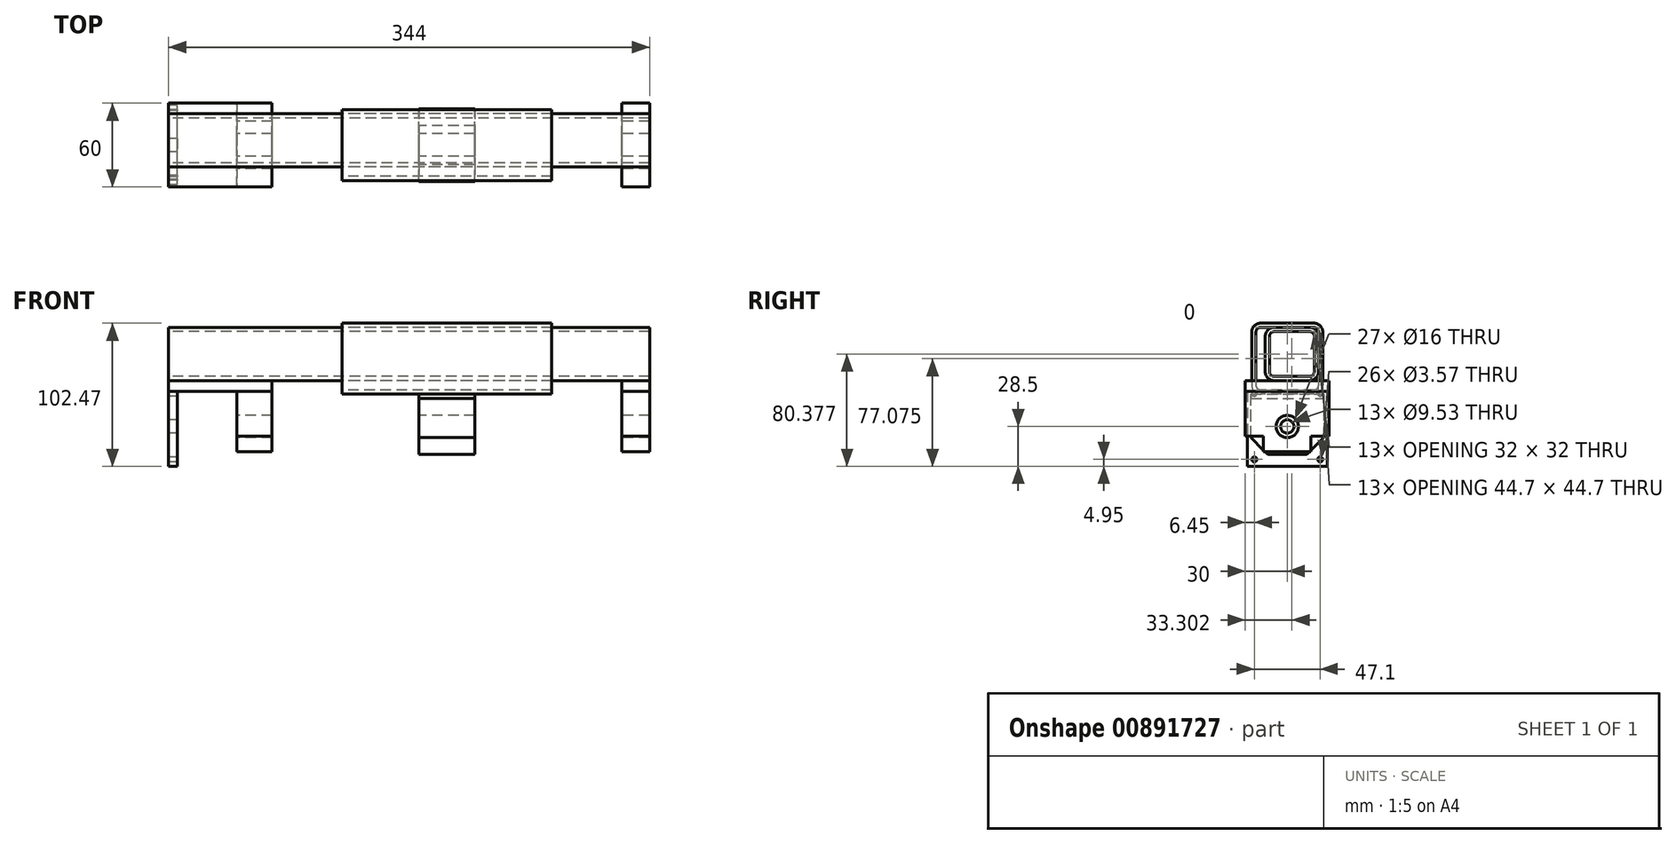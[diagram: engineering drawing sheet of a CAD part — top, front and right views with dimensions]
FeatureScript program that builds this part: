
annotation { "Feature Type Name" : "Feature", "Feature Type Description" : "" }
export const myFeature = defineFeature(function(context is Context, id is Id, definition is map)
    precondition{}
    {
        {
            var Q0;
            Q0=qCreatedBy(makeId("Right.planeOp"),FACE);
            var sketch = newSketch(context, id + "F0", { "sketchPlane" : qUnion([Q0])});
            skLineSegment(sketch, "E0", {"start": v(-26, 20) * mm, "end": v(26, 20) * mm});
            skLineSegment(sketch, "E1", {"start": v(26, 20) * mm, "end": v(26, -7.98) * mm});
            skLineSegment(sketch, "E2", {"start": v(26, -7.98) * mm, "end": v(13.98, -20) * mm});
            skLineSegment(sketch, "E3", {"start": v(13.98, -20) * mm, "end": v(-13.98, -20) * mm});
            skLineSegment(sketch, "E4", {"start": v(-13.98, -20) * mm, "end": v(-26, -7.98) * mm});
            skLineSegment(sketch, "E5", {"start": v(-26, -7.98) * mm, "end": v(-26, 20) * mm});
            skPoint(sketch, "E6", {"position": v(0, 0) * mm});
            skCircle(sketch, "E7", {"center": v(0, 0) * mm, "radius": 8 * mm});
            skSolve(sketch);
        }
        {
            var Q0;
            Q0=qCreatedBy(makeId("Right.planeOp"),FACE);
            var sketch = newSketch(context, id + "F1", { "sketchPlane" : qUnion([Q0])});
            skLineSegment(sketch, "E8.bottom", {"start": v(19.18, 70.93) * mm, "end": v(-19.18, 70.93) * mm});
            skLineSegment(sketch, "E8.top", {"start": v(19.18, 26.22) * mm, "end": v(-19.18, 26.22) * mm});
            skLineSegment(sketch, "E8.left", {"start": v(22.35, 67.75) * mm, "end": v(22.35, 29.4) * mm});
            skLineSegment(sketch, "E8.right", {"start": v(-22.35, 67.75) * mm, "end": v(-22.35, 29.4) * mm});
            skPoint(sketch, "E8.middle", {"position": v(0, 48.58) * mm});
            skLineSegment(sketch, "E9.bottom", {"start": v(19.05, 73.98) * mm, "end": v(-19.05, 73.98) * mm});
            skLineSegment(sketch, "E9.top", {"start": v(19.05, 23.18) * mm, "end": v(-19.05, 23.18) * mm});
            skLineSegment(sketch, "E9.left", {"start": v(25.4, 67.63) * mm, "end": v(25.4, 29.53) * mm});
            skLineSegment(sketch, "E9.right", {"start": v(-25.4, 67.63) * mm, "end": v(-25.4, 29.53) * mm});
            skPoint(sketch, "E10.visualSharp", {"position": v(-22.35, 70.93) * mm});
            skArc(sketch, "E10.filletArc", {"start": v(-19.18, 70.93) * mm, "mid": v(-21.42, 70) * mm, "end": v(-22.35, 67.75) * mm});
            skPoint(sketch, "E11.visualSharp", {"position": v(22.35, 70.93) * mm});
            skArc(sketch, "E11.filletArc", {"start": v(22.35, 67.75) * mm, "mid": v(21.42, 70) * mm, "end": v(19.18, 70.93) * mm});
            skPoint(sketch, "E12.visualSharp", {"position": v(22.35, 26.22) * mm});
            skArc(sketch, "E12.filletArc", {"start": v(19.18, 26.22) * mm, "mid": v(21.42, 27.15) * mm, "end": v(22.35, 29.4) * mm});
            skPoint(sketch, "E13.visualSharp", {"position": v(-22.35, 26.22) * mm});
            skArc(sketch, "E13.filletArc", {"start": v(-22.35, 29.4) * mm, "mid": v(-21.42, 27.15) * mm, "end": v(-19.18, 26.22) * mm});
            skPoint(sketch, "E14.visualSharp", {"position": v(-25.4, 73.98) * mm});
            skArc(sketch, "E14.filletArc", {"start": v(-19.05, 73.98) * mm, "mid": v(-23.54, 72.12) * mm, "end": v(-25.4, 67.63) * mm});
            skPoint(sketch, "E15.visualSharp", {"position": v(25.4, 73.98) * mm});
            skArc(sketch, "E15.filletArc", {"start": v(25.4, 67.63) * mm, "mid": v(23.54, 72.12) * mm, "end": v(19.05, 73.98) * mm});
            skPoint(sketch, "E16.visualSharp", {"position": v(25.4, 23.18) * mm});
            skArc(sketch, "E16.filletArc", {"start": v(19.05, 23.18) * mm, "mid": v(23.54, 25.03) * mm, "end": v(25.4, 29.53) * mm});
            skPoint(sketch, "E17.visualSharp", {"position": v(-25.4, 23.18) * mm});
            skArc(sketch, "E17.filletArc", {"start": v(-25.4, 29.53) * mm, "mid": v(-23.54, 25.03) * mm, "end": v(-19.05, 23.18) * mm});
            skLineSegment(sketch, "E18.bottom", {"start": v(-26, 23.18) * mm, "end": v(26, 23.18) * mm});
            skLineSegment(sketch, "E18.top", {"start": v(-26, 20) * mm, "end": v(26, 20) * mm});
            skLineSegment(sketch, "E18.left", {"start": v(-26, 23.18) * mm, "end": v(-26, 20) * mm});
            skLineSegment(sketch, "E18.right", {"start": v(26, 23.18) * mm, "end": v(26, 20) * mm});
            skSolve(sketch);
        }
        {
            var Q0;
            Q0=qCreatedBy(makeId("Right.planeOp"),FACE);
            var sketch = newSketch(context, id + "F2", { "sketchPlane" : qUnion([Q0])});
            skLineSegment(sketch, "E19.bottom", {"start": v(16.13, 67.88) * mm, "end": v(-9.52, 67.88) * mm});
            skLineSegment(sketch, "E19.top", {"start": v(16.13, 35.87) * mm, "end": v(-9.52, 35.87) * mm});
            skLineSegment(sketch, "E19.left", {"start": v(19.3, 64.7) * mm, "end": v(19.3, 39.05) * mm});
            skLineSegment(sketch, "E19.right", {"start": v(-12.7, 64.7) * mm, "end": v(-12.7, 39.05) * mm});
            skPoint(sketch, "E19.middle", {"position": v(3.3, 51.88) * mm});
            skLineSegment(sketch, "E20.bottom", {"start": v(16, 70.93) * mm, "end": v(-9.4, 70.93) * mm});
            skLineSegment(sketch, "E20.top", {"start": v(16, 32.83) * mm, "end": v(-9.4, 32.83) * mm});
            skLineSegment(sketch, "E20.left", {"start": v(22.35, 64.58) * mm, "end": v(22.35, 39.18) * mm});
            skLineSegment(sketch, "E20.right", {"start": v(-15.75, 64.58) * mm, "end": v(-15.75, 39.18) * mm});
            skPoint(sketch, "E21.visualSharp", {"position": v(-12.7, 67.88) * mm});
            skArc(sketch, "E21.filletArc", {"start": v(-9.52, 67.88) * mm, "mid": v(-11.77, 66.95) * mm, "end": v(-12.7, 64.7) * mm});
            skPoint(sketch, "E22.visualSharp", {"position": v(19.3, 67.88) * mm});
            skArc(sketch, "E22.filletArc", {"start": v(19.3, 64.7) * mm, "mid": v(18.37, 66.95) * mm, "end": v(16.13, 67.88) * mm});
            skPoint(sketch, "E23.visualSharp", {"position": v(19.3, 35.87) * mm});
            skArc(sketch, "E23.filletArc", {"start": v(16.13, 35.87) * mm, "mid": v(18.37, 36.8) * mm, "end": v(19.3, 39.05) * mm});
            skPoint(sketch, "E24.visualSharp", {"position": v(-12.7, 35.87) * mm});
            skArc(sketch, "E24.filletArc", {"start": v(-12.7, 39.05) * mm, "mid": v(-11.77, 36.8) * mm, "end": v(-9.52, 35.87) * mm});
            skPoint(sketch, "E25.visualSharp", {"position": v(-15.75, 70.93) * mm});
            skArc(sketch, "E25.filletArc", {"start": v(-9.4, 70.93) * mm, "mid": v(-13.89, 69.07) * mm, "end": v(-15.75, 64.58) * mm});
            skPoint(sketch, "E26.visualSharp", {"position": v(22.35, 70.93) * mm});
            skArc(sketch, "E26.filletArc", {"start": v(22.35, 64.58) * mm, "mid": v(20.5, 69.07) * mm, "end": v(16, 70.93) * mm});
            skPoint(sketch, "E27.visualSharp", {"position": v(22.35, 32.83) * mm});
            skArc(sketch, "E27.filletArc", {"start": v(16, 32.83) * mm, "mid": v(20.5, 34.69) * mm, "end": v(22.35, 39.18) * mm});
            skPoint(sketch, "E28.visualSharp", {"position": v(-15.75, 32.83) * mm});
            skArc(sketch, "E28.filletArc", {"start": v(-15.75, 39.18) * mm, "mid": v(-13.89, 34.69) * mm, "end": v(-9.4, 32.83) * mm});
            skSolve(sketch);
        }
        {
            var Q0;
            Q0=qCreatedBy(makeId("Right.planeOp"),FACE);
            var sketch = newSketch(context, id + "F3", { "sketchPlane" : qUnion([Q0])});
            skLineSegment(sketch, "E29", {"start": v(-30, 25) * mm, "end": v(-30, -7) * mm});
            skLineSegment(sketch, "E30", {"start": v(-30, -7) * mm, "end": v(-17, -7) * mm});
            skLineSegment(sketch, "E31", {"start": v(-17, -7) * mm, "end": v(-17, -18) * mm});
            skLineSegment(sketch, "E32", {"start": v(-17, -18) * mm, "end": v(17, -18) * mm});
            skLineSegment(sketch, "E33", {"start": v(17, -18) * mm, "end": v(17, -7) * mm});
            skLineSegment(sketch, "E34", {"start": v(17, -7) * mm, "end": v(30, -7) * mm});
            skLineSegment(sketch, "E35", {"start": v(30, 25) * mm, "end": v(30, -7) * mm});
            skPoint(sketch, "E36", {"position": v(0, 0) * mm});
            skLineSegment(sketch, "E37", {"start": v(30, 25) * mm, "end": v(-30, 25) * mm});
            skCircle(sketch, "E38", {"center": v(0, 0) * mm, "radius": 8 * mm});
            skLineSegment(sketch, "E39.top", {"start": v(30, 32.83) * mm, "end": v(-30, 32.83) * mm});
            skLineSegment(sketch, "E39.left", {"start": v(30, 25) * mm, "end": v(30, 32.83) * mm});
            skLineSegment(sketch, "E39.right", {"start": v(-30, 25) * mm, "end": v(-30, 32.83) * mm});
            skPoint(sketch, "E39.middle", {"position": v(0, 28.91) * mm});
            skSolve(sketch);
        }
        {
            var Q0;
            Q0=qCreatedBy(makeId("Right.planeOp"),FACE);
            var sketch = newSketch(context, id + "F4", { "sketchPlane" : qUnion([Q0])});
            skLineSegment(sketch, "E40.bottom", {"start": v(23.55, -23.55) * mm, "end": v(-23.55, -23.55) * mm, "construction": true});
            skLineSegment(sketch, "E40.top", {"start": v(23.55, 23.55) * mm, "end": v(-23.55, 23.55) * mm, "construction": true});
            skLineSegment(sketch, "E40.left", {"start": v(23.55, -23.55) * mm, "end": v(23.55, 23.55) * mm, "construction": true});
            skLineSegment(sketch, "E40.right", {"start": v(-23.55, -23.55) * mm, "end": v(-23.55, 23.55) * mm, "construction": true});
            skCircle(sketch, "E41", {"center": v(-23.55, -23.55) * mm, "radius": 1.79 * mm});
            skCircle(sketch, "E42", {"center": v(-23.55, 23.55) * mm, "radius": 1.79 * mm});
            skCircle(sketch, "E43", {"center": v(23.55, 23.55) * mm, "radius": 1.79 * mm});
            skCircle(sketch, "E44", {"center": v(23.55, -23.55) * mm, "radius": 1.79 * mm});
            skPoint(sketch, "E45.middle", {"position": v(0, 0) * mm});
            skCircle(sketch, "E46", {"center": v(0, 0) * mm, "radius": 4.76 * mm});
            skLineSegment(sketch, "E47", {"start": v(23.55, 23.55) * mm, "end": v(-23.55, -23.55) * mm, "construction": true});
            skLineSegment(sketch, "E48.bottom", {"start": v(28.5, 28.5) * mm, "end": v(-28.5, 28.5) * mm, "construction": true});
            skLineSegment(sketch, "E48.top", {"start": v(28.5, -28.5) * mm, "end": v(-28.5, -28.5) * mm, "construction": true});
            skLineSegment(sketch, "E48.left", {"start": v(28.5, 28.5) * mm, "end": v(28.5, -28.5) * mm, "construction": true});
            skLineSegment(sketch, "E48.right", {"start": v(-28.5, 28.5) * mm, "end": v(-28.5, -28.5) * mm, "construction": true});
            skLineSegment(sketch, "E49.bottom", {"start": v(-28.5, 25) * mm, "end": v(28.5, 25) * mm});
            skLineSegment(sketch, "E49.top", {"start": v(-28.5, -28.5) * mm, "end": v(28.5, -28.5) * mm});
            skLineSegment(sketch, "E49.left", {"start": v(-28.5, 25) * mm, "end": v(-28.5, -28.5) * mm});
            skLineSegment(sketch, "E49.right", {"start": v(28.5, 25) * mm, "end": v(28.5, -28.5) * mm});
            skPoint(sketch, "E50", {"position": v(0, 31.35) * mm});
            skPoint(sketch, "E50.positionSnap0", {"position": v(0, 28.5) * mm});
            skSolve(sketch);
        }
        {
            var Q0;
            Q0=qCreatedBy(makeId("Front.planeOp"),FACE);
            var sketch = newSketch(context, id + "F5", { "sketchPlane" : qUnion([Q0])});
            skPoint(sketch, "E51", {"position": v(6.35, 0) * mm});
            skPoint(sketch, "E52", {"position": v(49, 0) * mm});
            skPoint(sketch, "E53", {"position": v(74, 0) * mm});
            skPoint(sketch, "E54", {"position": v(124, 0) * mm});
            skPoint(sketch, "E55", {"position": v(274, 0) * mm});
            skPoint(sketch, "E56", {"position": v(179, 0) * mm});
            skPoint(sketch, "E57", {"position": v(219, 0) * mm});
            skPoint(sketch, "E58", {"position": v(324, 0) * mm});
            skPoint(sketch, "E59", {"position": v(344, 0) * mm});
            skSolve(sketch);
        }
        {
            var Q0;
            Q0=makeQuery(id+"F4.imprint","IMPRINT",FACE,{"disambiguationData":[TD([[makeQuery(id+"F4.imprint","IMPRINT",EDGE,{"derivedFrom":sQuery(id+"F4.wireOp",EDGE,"E41")}),-1.0]])]});
            var Q1;
            Q1=sQuery(id+"F5.wireOp",VERTEX,"E51");
            extrude(context, id + "F6", {"entities" : qUnion([Q0]), "endBound" : BoundingType.UP_TO_VERTEX, "depth" : 25 * mm, "endBoundEntityVertex" : qUnion([Q1]), "offsetDistance" : 25 * mm});
        }
        {
            var Q0;
            {var subQ0=sQuery(id+"F3.wireOp",EDGE,"E29");Q0=makeQuery(id+"F3.imprint","IMPRINT",FACE,{"disambiguationData":[TD([[makeQuery(id+"F3.imprint","IMPRINT",EDGE,{"derivedFrom":subQ0}),1.0]])]});}
            var Q1;
            Q1=sQuery(id+"F5.wireOp",VERTEX,"E53");
            var Q2;
            Q2=sQuery(id+"F5.wireOp",VERTEX,"E52");
            extrude(context, id + "F7", {"entities" : qUnion([Q0]), "endBound" : BoundingType.UP_TO_VERTEX, "depth" : 25 * mm, "endBoundEntityVertex" : qUnion([Q1]), "offsetDistance" : 25 * mm, "hasSecondDirection" : true, "secondDirectionBound" : BoundingType.UP_TO_VERTEX, "secondDirectionOppositeDirection" : false, "secondDirectionDepth" : 25 * mm, "secondDirectionBoundEntityVertex" : qUnion([Q2])});
        }
        {
            var Q0;
            Q0=makeQuery(id+"F1.imprint","IMPRINT",FACE,{"disambiguationData":[TD([[makeQuery(id+"F1.imprint","IMPRINT",EDGE,{"derivedFrom":sQuery(id+"F1.wireOp",EDGE,"E8.bottom")}),-1.0]])]});
            var Q1;
            Q1=sQuery(id+"F5.wireOp",VERTEX,"E55");
            var Q2;
            Q2=sQuery(id+"F5.wireOp",VERTEX,"E54");
            extrude(context, id + "F8", {"entities" : qUnion([Q0]), "endBound" : BoundingType.UP_TO_VERTEX, "depth" : 25 * mm, "endBoundEntityVertex" : qUnion([Q1]), "offsetDistance" : 25 * mm, "hasSecondDirection" : true, "secondDirectionBound" : BoundingType.UP_TO_VERTEX, "secondDirectionOppositeDirection" : false, "secondDirectionDepth" : 25 * mm, "secondDirectionBoundEntityVertex" : qUnion([Q2])});
        }
        {
            var Q0;
            Q0=makeQuery(id+"F2.imprint","IMPRINT",FACE,{"disambiguationData":[TD([[makeQuery(id+"F2.imprint","IMPRINT",EDGE,{"derivedFrom":sQuery(id+"F2.wireOp",EDGE,"E19.bottom")}),-1.0]])]});
            var Q1;
            Q1=sQuery(id+"F5.wireOp",VERTEX,"E59");
            extrude(context, id + "F9", {"entities" : qUnion([Q0]), "endBound" : BoundingType.UP_TO_VERTEX, "depth" : 25 * mm, "endBoundEntityVertex" : qUnion([Q1]), "offsetDistance" : 25 * mm});
        }
        {
            var Q0;
            Q0=makeQuery(id+"F0.imprint","IMPRINT",FACE,{"disambiguationData":[TD([[makeQuery(id+"F0.imprint","IMPRINT",EDGE,{"derivedFrom":sQuery(id+"F0.wireOp",EDGE,"E0")}),-1.0]])]});
            var Q1;
            Q1=sQuery(id+"F5.wireOp",VERTEX,"E57");
            var Q2;
            Q2=sQuery(id+"F5.wireOp",VERTEX,"E56");
            extrude(context, id + "F10", {"entities" : qUnion([Q0]), "operationType" : NewBodyOperationType.ADD, "endBound" : BoundingType.UP_TO_VERTEX, "depth" : 25 * mm, "endBoundEntityVertex" : qUnion([Q1]), "offsetDistance" : 25 * mm, "hasSecondDirection" : true, "secondDirectionBound" : BoundingType.UP_TO_VERTEX, "secondDirectionOppositeDirection" : false, "secondDirectionDepth" : 25 * mm, "secondDirectionBoundEntityVertex" : qUnion([Q2])});
        }
        {
            var Q0;
            Q0=makeQuery(id+"F3.imprint","IMPRINT",FACE,{"disambiguationData":[TD([[makeQuery(id+"F3.imprint","IMPRINT",EDGE,{"derivedFrom":sQuery(id+"F3.wireOp",EDGE,"E39.top")}),1.0]])]});
            var Q1;
            Q1=sQuery(id+"F5.wireOp",VERTEX,"E53");
            extrude(context, id + "F11", {"entities" : qUnion([Q0]), "endBound" : BoundingType.UP_TO_VERTEX, "depth" : 25 * mm, "endBoundEntityVertex" : qUnion([Q1]), "offsetDistance" : 25 * mm});
        }
        {
            var Q0;
            {var subQ0=sQuery(id+"F3.wireOp",EDGE,"E29");Q0=makeQuery(id+"F3.imprint","IMPRINT",FACE,{"disambiguationData":[TD([[makeQuery(id+"F3.imprint","IMPRINT",EDGE,{"derivedFrom":subQ0}),1.0]])]});}
            var Q1;
            Q1=sQuery(id+"F5.wireOp",VERTEX,"E59");
            var Q2;
            Q2=sQuery(id+"F5.wireOp",VERTEX,"E58");
            extrude(context, id + "F12", {"entities" : qUnion([Q0]), "endBound" : BoundingType.UP_TO_VERTEX, "depth" : 25 * mm, "endBoundEntityVertex" : qUnion([Q1]), "offsetDistance" : 25 * mm, "hasSecondDirection" : true, "secondDirectionBound" : BoundingType.UP_TO_VERTEX, "secondDirectionOppositeDirection" : false, "secondDirectionDepth" : 25 * mm, "secondDirectionBoundEntityVertex" : qUnion([Q2])});
        }
        {
            var Q0;
            Q0=makeQuery(id+"F3.imprint","IMPRINT",FACE,{"disambiguationData":[TD([[makeQuery(id+"F3.imprint","IMPRINT",EDGE,{"derivedFrom":sQuery(id+"F3.wireOp",EDGE,"E39.top")}),1.0]])]});
            var Q1;
            Q1=sQuery(id+"F5.wireOp",VERTEX,"E59");
            var Q2;
            Q2=sQuery(id+"F5.wireOp",VERTEX,"E58");
            extrude(context, id + "F13", {"entities" : qUnion([Q0]), "endBound" : BoundingType.UP_TO_VERTEX, "depth" : 25 * mm, "endBoundEntityVertex" : qUnion([Q1]), "offsetDistance" : 25 * mm, "hasSecondDirection" : true, "secondDirectionBound" : BoundingType.UP_TO_VERTEX, "secondDirectionOppositeDirection" : false, "secondDirectionDepth" : 25 * mm, "secondDirectionBoundEntityVertex" : qUnion([Q2])});
        }
        {
            var Q0;
            {var subQ1=sQuery(id+"F1.wireOp",EDGE,"E9.top");Q0=makeQuery(id+"F1.imprint","IMPRINT",FACE,{"disambiguationData":[TD([[makeQuery(id+"F1.imprint","IMPRINT",EDGE,{"derivedFrom":subQ1}),1.0]])]});}
            var Q1;
            Q1=sQuery(id+"F5.wireOp",VERTEX,"E57");
            var Q2;
            Q2=sQuery(id+"F5.wireOp",VERTEX,"E56");
            extrude(context, id + "F14", {"entities" : qUnion([Q0]), "endBound" : BoundingType.UP_TO_VERTEX, "depth" : 25 * mm, "endBoundEntityVertex" : qUnion([Q1]), "offsetDistance" : 25 * mm, "hasSecondDirection" : true, "secondDirectionBound" : BoundingType.UP_TO_VERTEX, "secondDirectionOppositeDirection" : false, "secondDirectionDepth" : 25 * mm, "secondDirectionBoundEntityVertex" : qUnion([Q2])});
        }
    });
